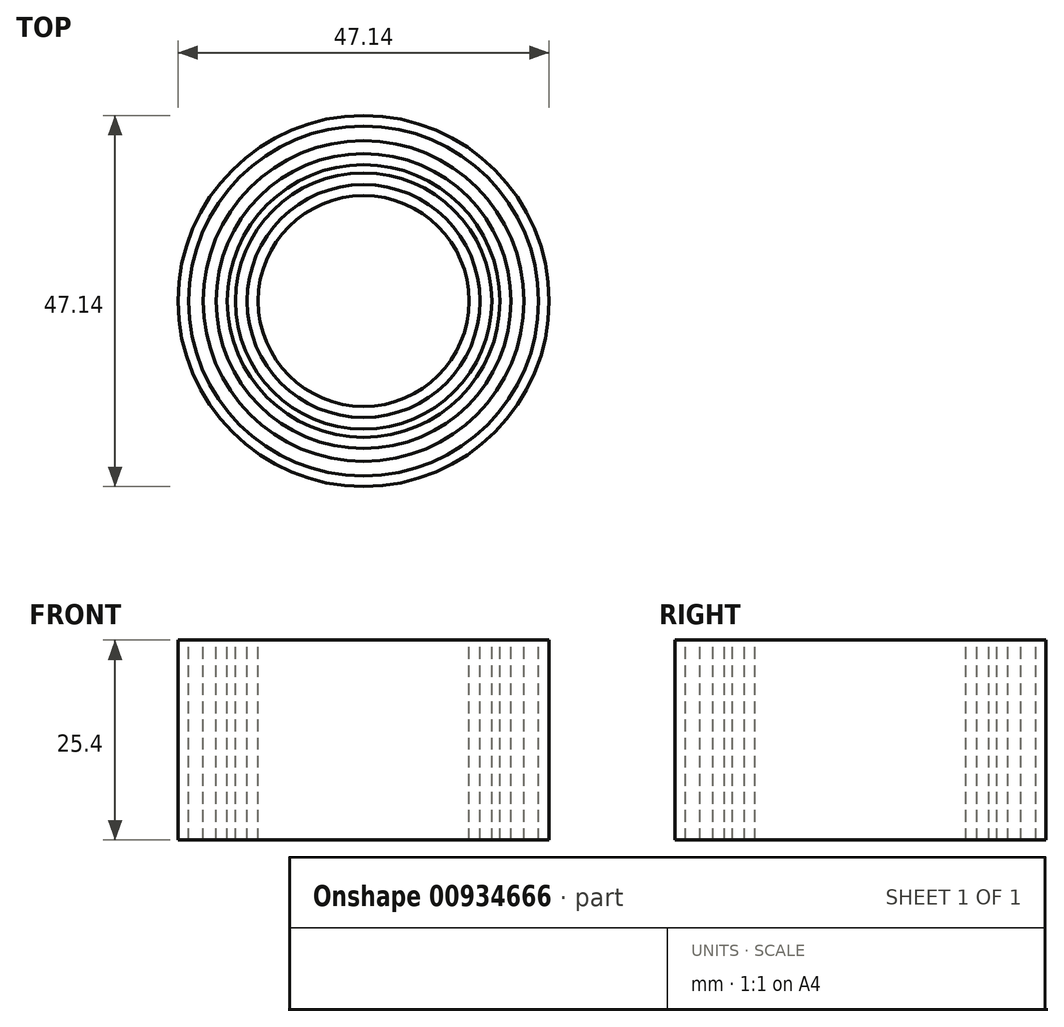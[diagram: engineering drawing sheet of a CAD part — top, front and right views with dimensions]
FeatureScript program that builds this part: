
annotation { "Feature Type Name" : "Feature", "Feature Type Description" : "" }
export const myFeature = defineFeature(function(context is Context, id is Id, definition is map)
    precondition{}
    {
        {
            var Q0;
            Q0=qCreatedBy(makeId("Top.planeOp"),FACE);
            var sketch = newSketch(context, id + "F0", { "sketchPlane" : qUnion([Q0])});
            skCircle(sketch, "E0", {"center": v(0, 0) * mm, "radius": 23.57 * mm});
            skCircle(sketch, "E1", {"center": v(0, 0) * mm, "radius": 22.24 * mm});
            skCircle(sketch, "E2", {"center": v(0, 0) * mm, "radius": 20.38 * mm});
            skCircle(sketch, "E3", {"center": v(0, 0) * mm, "radius": 18.73 * mm});
            skCircle(sketch, "E4", {"center": v(0, 0) * mm, "radius": 17.32 * mm});
            skCircle(sketch, "E5", {"center": v(0, 0) * mm, "radius": 16.28 * mm});
            skCircle(sketch, "E6", {"center": v(0, 0) * mm, "radius": 14.79 * mm});
            skCircle(sketch, "E7", {"center": v(0, 0) * mm, "radius": 13.4 * mm});
            skSolve(sketch);
        }
        {
            var Q0;
            Q0=sQuery(id+"F0.wireOp",EDGE,"E7");
            var Q1;
            Q1=sQuery(id+"F0.wireOp",EDGE,"E6");
            var Q2;
            Q2=sQuery(id+"F0.wireOp",EDGE,"E5");
            var Q3;
            Q3=sQuery(id+"F0.wireOp",EDGE,"E3");
            var Q4;
            Q4=sQuery(id+"F0.wireOp",EDGE,"E4");
            var Q5;
            Q5=sQuery(id+"F0.wireOp",EDGE,"E2");
            var Q6;
            Q6=sQuery(id+"F0.wireOp",EDGE,"E1");
            var Q7;
            Q7=sQuery(id+"F0.wireOp",EDGE,"E0");
            extrude(context, id + "F1", {"bodyType" : ToolBodyType.SURFACE, "surfaceEntities" : qUnion([Q0, Q1, Q2, Q3, Q4, Q5, Q6, Q7]), "depth" : 25.4 * mm, "offsetDistance" : 25.4 * mm});
        }
    });
